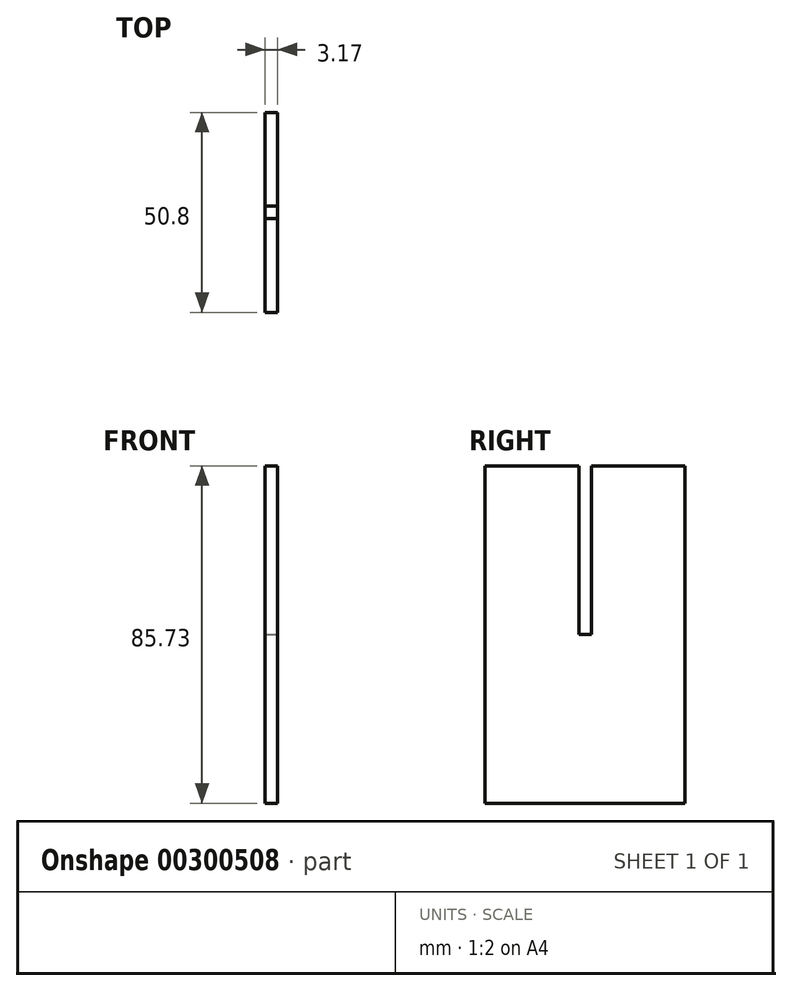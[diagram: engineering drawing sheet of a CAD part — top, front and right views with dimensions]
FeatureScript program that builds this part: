
annotation { "Feature Type Name" : "Feature", "Feature Type Description" : "" }
export const myFeature = defineFeature(function(context is Context, id is Id, definition is map)
    precondition{}
    {
        {
            var Q0;
            Q0=qCreatedBy(makeId("Right.planeOp"),FACE);
            var sketch = newSketch(context, id + "F0", { "sketchPlane" : qUnion([Q0])});
            skLineSegment(sketch, "E0.bottom", {"start": v(-126.06, -58.01) * mm, "end": v(-75.26, -58.01) * mm});
            skLineSegment(sketch, "E0.top", {"start": v(-126.06, -143.74) * mm, "end": v(-75.26, -143.74) * mm});
            skLineSegment(sketch, "E0.left", {"start": v(-126.06, -58.01) * mm, "end": v(-126.06, -143.74) * mm});
            skLineSegment(sketch, "E0.right", {"start": v(-75.26, -58.01) * mm, "end": v(-75.26, -143.74) * mm});
            skSolve(sketch);
        }
        {
            var Q0;
            Q0=makeQuery(id+"F0.imprint","IMPRINT",FACE,{"disambiguationData":[TD([[makeQuery(id+"F0.imprint","IMPRINT",EDGE,{"derivedFrom":sQuery(id+"F0.wireOp",EDGE,"E0.bottom")}),-1.0]])]});
            extrude(context, id + "F1", {"entities" : qUnion([Q0]), "depth" : 3.17 * mm});
        }
        {
            var Q0;
            Q0=makeQuery(id+"F1.opExtrude","CAP_FACE",FACE,{"disambiguationData":[OSD([sQuery(id+"F0.wireOp",EDGE,"E0.bottom"),sQuery(id+"F0.wireOp",EDGE,"E0.top"),sQuery(id+"F0.wireOp",EDGE,"E0.left"),sQuery(id+"F0.wireOp",EDGE,"E0.right")])],"isStart":false});
            var sketch = newSketch(context, id + "F2", { "sketchPlane" : qUnion([Q0])});
            skLineSegment(sketch, "E1", {"start": v(-100.66, -58.01) * mm, "end": v(-100.66, -143.74) * mm});
            skLineSegment(sketch, "E2.bottom", {"start": v(-100.66, -58.01) * mm, "end": v(-102.25, -58.01) * mm});
            skLineSegment(sketch, "E2.top", {"start": v(-100.66, -100.89) * mm, "end": v(-102.25, -100.89) * mm});
            skLineSegment(sketch, "E2.left", {"start": v(-100.66, -58.01) * mm, "end": v(-100.66, -100.89) * mm});
            skLineSegment(sketch, "E2.right", {"start": v(-102.25, -58.01) * mm, "end": v(-102.25, -100.89) * mm});
            skLineSegment(sketch, "E3.bottom", {"start": v(-100.66, -58.01) * mm, "end": v(-99.07, -58.01) * mm});
            skLineSegment(sketch, "E3.top", {"start": v(-100.66, -100.89) * mm, "end": v(-99.07, -100.89) * mm});
            skLineSegment(sketch, "E3.right", {"start": v(-99.07, -58.01) * mm, "end": v(-99.07, -100.89) * mm});
            skSolve(sketch);
        }
        {
            var Q0;
            Q0=makeQuery(id+"F2.imprint","IMPRINT",FACE,{"disambiguationData":[TD([[makeQuery(id+"F2.imprint","IMPRINT",EDGE,{"derivedFrom":sQuery(id+"F2.wireOp",EDGE,"E2.bottom")}),-1.0]])]});
            var Q1;
            Q1=makeQuery(id+"F2.imprint","IMPRINT",FACE,{"disambiguationData":[TD([[makeQuery(id+"F2.imprint","IMPRINT",EDGE,{"derivedFrom":sQuery(id+"F2.wireOp",EDGE,"E3.bottom")}),-1.0]])]});
            extrude(context, id + "F3", {"entities" : qUnion([Q0, Q1]), "operationType" : NewBodyOperationType.REMOVE, "endBound" : BoundingType.THROUGH_ALL, "oppositeDirection" : true, "depth" : 25.4 * mm});
        }
    });
